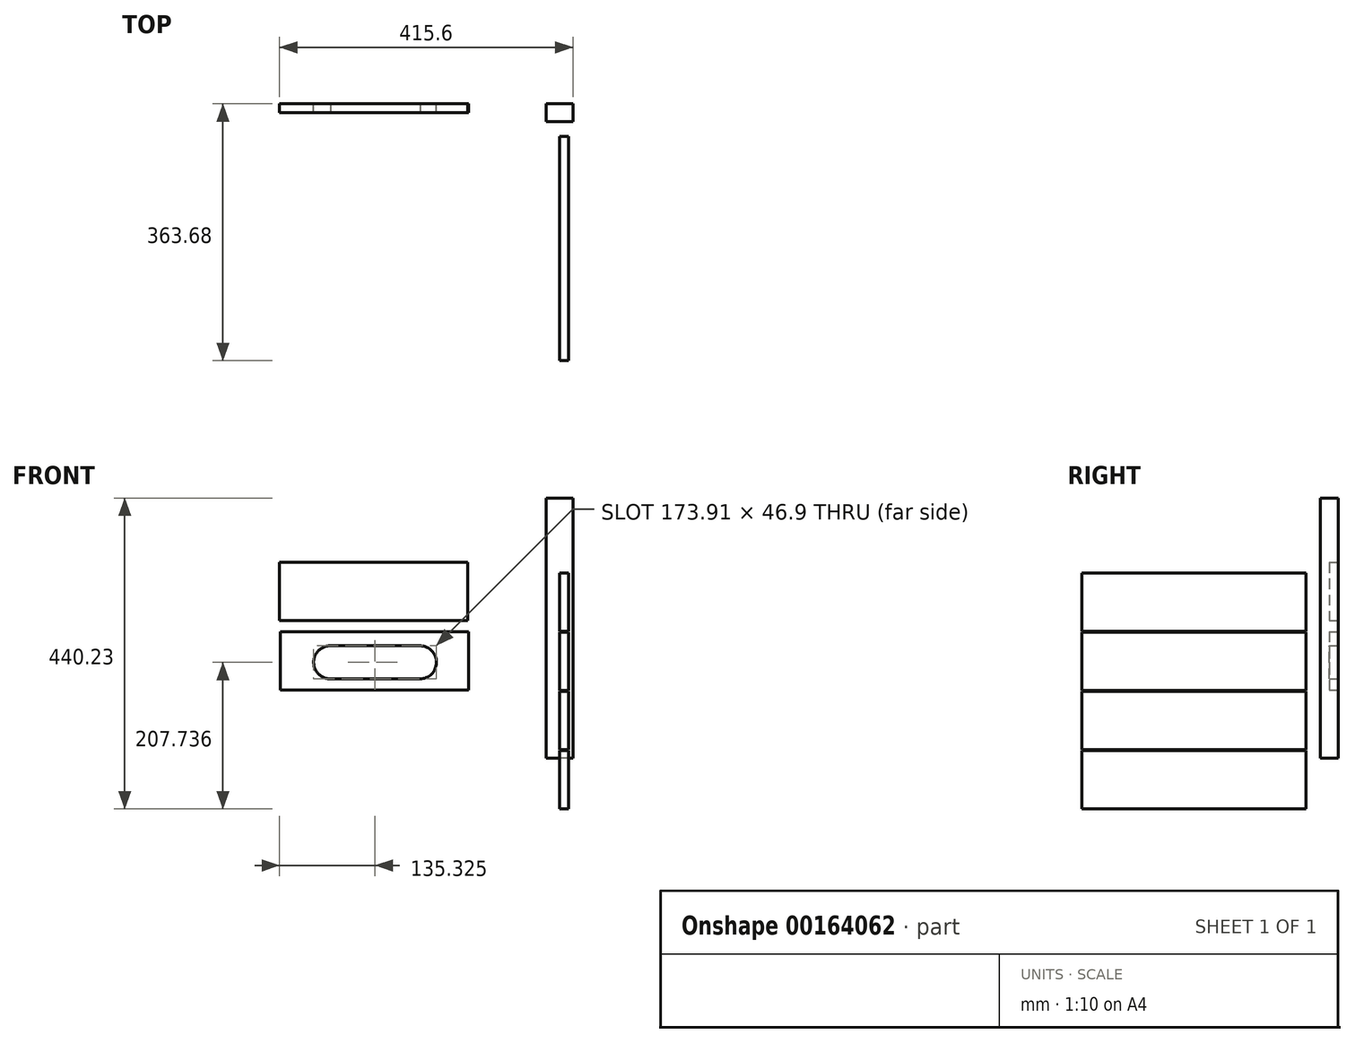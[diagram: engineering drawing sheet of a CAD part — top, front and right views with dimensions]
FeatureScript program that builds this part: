
annotation { "Feature Type Name" : "Feature", "Feature Type Description" : "" }
export const myFeature = defineFeature(function(context is Context, id is Id, definition is map)
    precondition{}
    {
        {
            var Q0;
            Q0=qCreatedBy(makeId("Front.planeOp"),FACE);
            var sketch = newSketch(context, id + "F0", { "sketchPlane" : qUnion([Q0])});
            skLineSegment(sketch, "E0.bottom", {"start": v(19.05, 184.15) * mm, "end": v(-19.05, 184.15) * mm});
            skLineSegment(sketch, "E0.top", {"start": v(19.05, -184.15) * mm, "end": v(-19.05, -184.15) * mm});
            skLineSegment(sketch, "E0.left", {"start": v(19.05, 184.15) * mm, "end": v(19.05, -184.15) * mm});
            skLineSegment(sketch, "E0.right", {"start": v(-19.05, 184.15) * mm, "end": v(-19.05, -184.15) * mm});
            skPoint(sketch, "E0.middle", {"position": v(0, 0) * mm});
            skSolve(sketch);
        }
        {
            var Q0;
            Q0=makeQuery(id+"F0.imprint","IMPRINT",FACE,{"disambiguationData":[TD([[makeQuery(id+"F0.imprint","IMPRINT",EDGE,{"derivedFrom":sQuery(id+"F0.wireOp",EDGE,"E0.bottom")}),1.0]])]});
            extrude(context, id + "F1", {"entities" : qUnion([Q0]), "depth" : 25.4 * mm});
        }
        {
            var Q0;
            Q0=qCreatedBy(makeId("Front.planeOp"),FACE);
            var sketch = newSketch(context, id + "F2", { "sketchPlane" : qUnion([Q0])});
            skLineSegment(sketch, "E1.bottom", {"start": v(-129.85, 93.33) * mm, "end": v(-396.55, 93.33) * mm});
            skLineSegment(sketch, "E1.top", {"start": v(-129.85, 10.78) * mm, "end": v(-396.55, 10.78) * mm});
            skLineSegment(sketch, "E1.left", {"start": v(-129.85, 93.33) * mm, "end": v(-129.85, 10.78) * mm});
            skLineSegment(sketch, "E1.right", {"start": v(-396.55, 93.33) * mm, "end": v(-396.55, 10.78) * mm});
            skSolve(sketch);
        }
        {
            var Q0;
            Q0 = qSketchRegion(id + "F2", true);
            extrude(context, id + "F3", {"entities" : qUnion([Q0]), "depth" : 12.7 * mm});
        }
        {
            var Q0;
            Q0=qCreatedBy(makeId("Front.planeOp"),FACE);
            var sketch = newSketch(context, id + "F4", { "sketchPlane" : qUnion([Q0])});
            skLineSegment(sketch, "E2.bottom", {"start": v(-128.36, -4.81) * mm, "end": v(-395.06, -4.81) * mm});
            skLineSegment(sketch, "E2.top", {"start": v(-128.36, -87.36) * mm, "end": v(-395.06, -87.36) * mm});
            skLineSegment(sketch, "E2.left", {"start": v(-128.36, -4.81) * mm, "end": v(-128.36, -87.36) * mm});
            skLineSegment(sketch, "E2.right", {"start": v(-395.06, -4.81) * mm, "end": v(-395.06, -87.36) * mm});
            skLineSegment(sketch, "E3", {"start": v(-323.92, -24.9) * mm, "end": v(-196.92, -24.9) * mm});
            skLineSegment(sketch, "E4", {"start": v(-324.72, -71.8) * mm, "end": v(-197.72, -71.8) * mm});
            skLineSegment(sketch, "E5", {"start": v(-261.71, -4.81) * mm, "end": v(-261.71, -87.36) * mm, "construction": true});
            skPoint(sketch, "E6", {"position": v(-260.42, -24.9) * mm});
            skPoint(sketch, "E7", {"position": v(-395.06, -46.09) * mm});
            skArc(sketch, "E8", {"start": v(-323.92, -24.9) * mm, "mid": v(-348.18, -47.93) * mm, "end": v(-324.72, -71.8) * mm});
            skArc(sketch, "E9", {"start": v(-197.72, -71.8) * mm, "mid": v(-174.27, -48.74) * mm, "end": v(-196.92, -24.9) * mm});
            skLineSegment(sketch, "E10", {"start": v(-197.72, -71.8) * mm, "end": v(-324.72, -71.8) * mm});
            skSolve(sketch);
        }
        {
            var Q0;
            Q0=makeQuery(id+"F4.imprint","IMPRINT",FACE,{"disambiguationData":[TD([[makeQuery(id+"F4.imprint","IMPRINT",EDGE,{"derivedFrom":sQuery(id+"F4.wireOp",EDGE,"E2.bottom")}),1.0]])]});
            extrude(context, id + "F5", {"entities" : qUnion([Q0]), "depth" : 12.7 * mm});
        }
        {
            var Q0;
            Q0=qCreatedBy(makeId("Right.planeOp"),FACE);
            var sketch = newSketch(context, id + "F6", { "sketchPlane" : qUnion([Q0])});
            skLineSegment(sketch, "E11.bottom", {"start": v(-363.68, 77.93) * mm, "end": v(-46.18, 77.93) * mm});
            skLineSegment(sketch, "E11.top", {"start": v(-363.68, -4.62) * mm, "end": v(-46.18, -4.62) * mm});
            skLineSegment(sketch, "E11.left", {"start": v(-363.68, 77.93) * mm, "end": v(-363.68, -4.62) * mm});
            skLineSegment(sketch, "E11.right", {"start": v(-46.18, 77.93) * mm, "end": v(-46.18, -4.62) * mm});
            skLineSegment(sketch, "E12.0.0.1", {"start": v(-363.68, -5.89) * mm, "end": v(-363.68, -88.44) * mm});
            skLineSegment(sketch, "E12.1.0.1", {"start": v(-363.68, -5.89) * mm, "end": v(-46.18, -5.89) * mm});
            skLineSegment(sketch, "E12.2.0.1", {"start": v(-363.68, -88.44) * mm, "end": v(-46.18, -88.44) * mm});
            skLineSegment(sketch, "E12.3.0.1", {"start": v(-46.18, -5.89) * mm, "end": v(-46.18, -88.44) * mm});
            skLineSegment(sketch, "E12.0.0.2", {"start": v(-363.68, -89.7) * mm, "end": v(-363.68, -172.26) * mm});
            skLineSegment(sketch, "E12.1.0.2", {"start": v(-363.68, -89.7) * mm, "end": v(-46.18, -89.7) * mm});
            skLineSegment(sketch, "E12.2.0.2", {"start": v(-363.68, -172.26) * mm, "end": v(-46.18, -172.26) * mm});
            skLineSegment(sketch, "E12.3.0.2", {"start": v(-46.18, -89.7) * mm, "end": v(-46.18, -172.26) * mm});
            skLineSegment(sketch, "E12.0.0.3", {"start": v(-363.68, -173.53) * mm, "end": v(-363.68, -256.08) * mm});
            skLineSegment(sketch, "E12.1.0.3", {"start": v(-363.68, -173.53) * mm, "end": v(-46.18, -173.53) * mm});
            skLineSegment(sketch, "E12.2.0.3", {"start": v(-363.68, -256.08) * mm, "end": v(-46.18, -256.08) * mm});
            skLineSegment(sketch, "E12.3.0.3", {"start": v(-46.18, -173.53) * mm, "end": v(-46.18, -256.08) * mm});
            skLineSegment(sketch, "E12.direction1", {"start": v(-363.68, -4.62) * mm, "end": v(-338.28, -4.62) * mm, "construction": true});
            skLineSegment(sketch, "E12.direction2", {"start": v(-363.68, -4.62) * mm, "end": v(-363.68, -88.44) * mm, "construction": true});
            skSolve(sketch);
        }
        {
            var Q0;
            Q0 = qSketchRegion(id + "F6", true);
            extrude(context, id + "F7", {"entities" : qUnion([Q0]), "depth" : 12.7 * mm});
        }
    });
